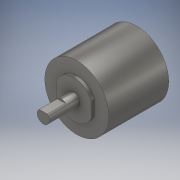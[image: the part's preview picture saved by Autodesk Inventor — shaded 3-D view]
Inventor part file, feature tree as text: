
AUTODESK INVENTOR PART (.ipt)
format: ipt  version: 2019 (Build 230136000, 136)  size: 134,656 bytes
history: native  units: mm
features: extrude x5, sketch x5, other x1
ambient origin geometry x8: Origin, YZ Plane, XZ Plane, XY Plane, X Axis, Y Axis, Z Axis, Center Point
bodies: Body1 (feature_tree)
feature tree (11):
  other  "ソリッド1"
  extrude  "押し出し1"  Depth=42.0mm
  extrude  "押し出し2"  Depth=39.2mm TaperAngle=0.0deg
  extrude  "押し出し3"  Depth=25.0mm
  extrude  "押し出し4"  Depth=2.0mm TaperAngle=0.0deg
  extrude  "押し出し5"  Depth=8.0mm
  sketch  "スケッチ1"
  sketch  "スケッチ2"
  sketch  "スケッチ3"
  sketch  "スケッチ4"
  sketch  "スケッチ5"
